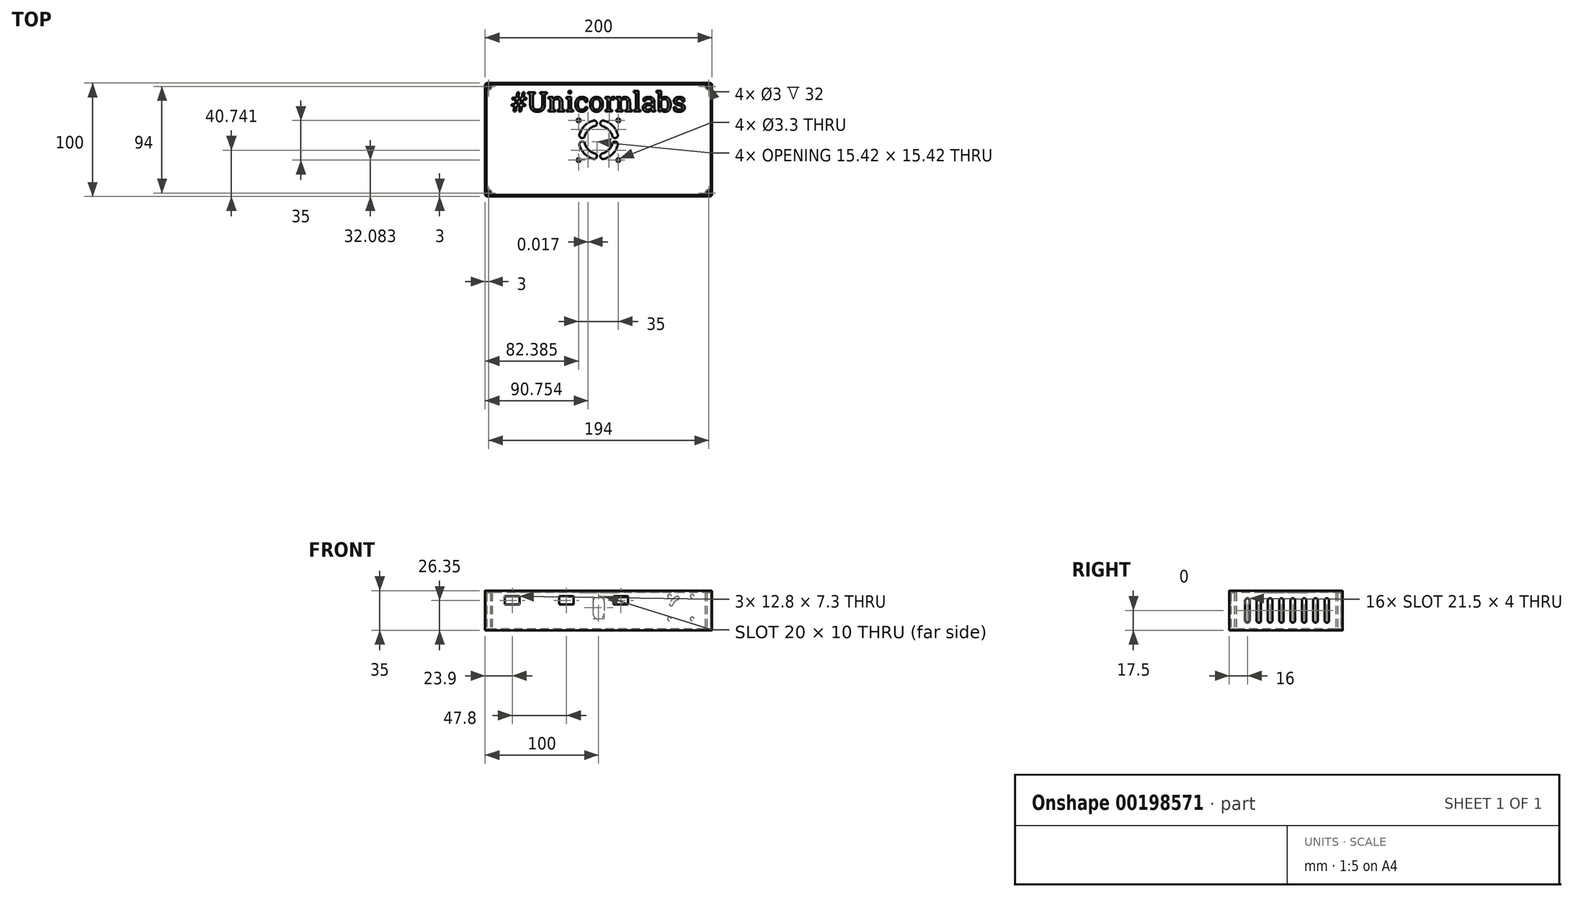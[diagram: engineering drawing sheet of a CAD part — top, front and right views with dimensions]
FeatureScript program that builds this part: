
annotation { "Feature Type Name" : "Feature", "Feature Type Description" : "" }
export const myFeature = defineFeature(function(context is Context, id is Id, definition is map)
    precondition{}
    {
        {
            assignVariable(context, id + "F0", {"name" : "CaseHeight", "anyValue" : 35});
        }
        {
            assignVariable(context, id + "F1", {"name" : "CaseWallThickness", "anyValue" : 1.2});
        }
        {
            assignVariable(context, id + "F2", {"name" : "MetricScrew", "anyValue" : 3});
        }
        {
            var Q0;
            Q0=qCreatedBy(makeId("Top.planeOp"),FACE);
            var sketch = newSketch(context, id + "F3", { "sketchPlane" : qUnion([Q0])});
            skLineSegment(sketch, "E0.bottom", {"start": v(100, 50) * mm, "end": v(-100, 50) * mm});
            skLineSegment(sketch, "E0.top", {"start": v(100, -50) * mm, "end": v(-100, -50) * mm});
            skLineSegment(sketch, "E0.left", {"start": v(100, 50) * mm, "end": v(100, -50) * mm});
            skLineSegment(sketch, "E0.right", {"start": v(-100, 50) * mm, "end": v(-100, -50) * mm});
            skPoint(sketch, "E0.middle", {"position": v(0, 0) * mm});
            skSolve(sketch);
        }
        {
            var Q0;
            Q0=makeQuery(id+"F3.imprint","IMPRINT",FACE,{"disambiguationData":[TD([[makeQuery(id+"F3.imprint","IMPRINT",EDGE,{"derivedFrom":sQuery(id+"F3.wireOp",EDGE,"E0.bottom")}),1.0]])]});
            extrude(context, id + "F4", {"entities" : qUnion([Q0]), "depth" : (getVariable(context, 'CaseHeight')) * mm});
        }
        {
            var Q0;
            Q0=makeQuery(id+"F4.opExtrude","CAP_FACE",FACE,{"disambiguationData":[OSD([sQuery(id+"F3.wireOp",EDGE,"E0.bottom"),sQuery(id+"F3.wireOp",EDGE,"E0.top"),sQuery(id+"F3.wireOp",EDGE,"E0.left"),sQuery(id+"F3.wireOp",EDGE,"E0.right")])],"isStart":false});
            shell(context, id + "F5", {"entities" : qUnion([Q0]), "thickness" : (getVariable(context, 'CaseWallThickness')) * mm});
        }
        {
            var Q0;
            Q0=makeQuery(id+"F5.opShell","OFFSET_FACE",FACE,{"disambiguationData":[OSD([sQuery(id+"F3.wireOp",EDGE,"E0.bottom"),sQuery(id+"F3.wireOp",EDGE,"E0.top"),sQuery(id+"F3.wireOp",EDGE,"E0.left"),sQuery(id+"F3.wireOp",EDGE,"E0.right")])]});
            var sketch = newSketch(context, id + "F6", { "sketchPlane" : qUnion([Q0])});
            skCircle(sketch, "E1", {"center": v(-97, 47) * mm, "radius": 1.5 * mm});
            skCircle(sketch, "E2", {"center": v(97, 47) * mm, "radius": 1.5 * mm});
            skCircle(sketch, "E3", {"center": v(97, -47) * mm, "radius": 1.5 * mm});
            skCircle(sketch, "E4", {"center": v(-97, -47) * mm, "radius": 1.5 * mm});
            skArc(sketch, "E5", {"start": v(-98.8, 44) * mm, "mid": v(-94.88, 44.88) * mm, "end": v(-94, 48.8) * mm});
            skArc(sketch, "E6.MirrorCS", {"start": v(98.8, 44) * mm, "mid": v(94.88, 44.88) * mm, "end": v(94, 48.8) * mm});
            skArc(sketch, "E7.MirrorCS", {"start": v(-98.8, -44) * mm, "mid": v(-94.88, -44.88) * mm, "end": v(-94, -48.8) * mm});
            skArc(sketch, "E8.MirrorCS", {"start": v(98.8, -44) * mm, "mid": v(94.88, -44.88) * mm, "end": v(94, -48.8) * mm});
            skSolve(sketch);
        }
        {
            var Q0;
            Q0=makeQuery(id+"F6.imprint","IMPRINT",FACE,{"disambiguationData":[TD([[makeQuery(id+"F6.imprint","IMPRINT",EDGE,{"derivedFrom":sQuery(id+"F6.wireOp",EDGE,"E1")}),-1.0]])]});
            var Q1;
            Q1=makeQuery(id+"F6.imprint","IMPRINT",FACE,{"disambiguationData":[TD([[makeQuery(id+"F6.imprint","IMPRINT",EDGE,{"derivedFrom":sQuery(id+"F6.wireOp",EDGE,"E2")}),-1.0]])]});
            var Q2;
            Q2=makeQuery(id+"F6.imprint","IMPRINT",FACE,{"disambiguationData":[TD([[makeQuery(id+"F6.imprint","IMPRINT",EDGE,{"derivedFrom":sQuery(id+"F6.wireOp",EDGE,"E3")}),-1.0]])]});
            var Q3;
            Q3=makeQuery(id+"F6.imprint","IMPRINT",FACE,{"disambiguationData":[TD([[makeQuery(id+"F6.imprint","IMPRINT",EDGE,{"derivedFrom":sQuery(id+"F6.wireOp",EDGE,"E4")}),-1.0]])]});
            extrude(context, id + "F7", {"entities" : qUnion([Q0, Q1, Q2, Q3]), "operationType" : NewBodyOperationType.ADD, "depth" : (getVariable(context, 'CaseHeight') - getVariable(context, 'MetricScrew')) * mm});
        }
        {
            var Q0;
            Q0=makeQuery(id+"F7.opExtrude","CAP_FACE",FACE,{"disambiguationData":[OSD([sQuery(id+"F3.wireOp",EDGE,"E0.bottom"),sQuery(id+"F3.wireOp",EDGE,"E0.right"),sQuery(id+"F6.wireOp",EDGE,"E1"),sQuery(id+"F6.wireOp",EDGE,"E5")])],"isStart":false});
            var sketch = newSketch(context, id + "F8", { "sketchPlane" : qUnion([Q0])});
            skPoint(sketch, "E9.0", {"position": v(98.8, -48.8) * mm});
            skPoint(sketch, "E10.0", {"position": v(-98.8, 48.8) * mm});
            skLineSegment(sketch, "E11.bottom", {"start": v(-98.8, 48.8) * mm, "end": v(98.8, 48.8) * mm});
            skLineSegment(sketch, "E11.top", {"start": v(-98.8, -48.8) * mm, "end": v(98.8, -48.8) * mm});
            skLineSegment(sketch, "E11.left", {"start": v(-98.8, 48.8) * mm, "end": v(-98.8, -48.8) * mm});
            skLineSegment(sketch, "E11.right", {"start": v(98.8, 48.8) * mm, "end": v(98.8, -48.8) * mm});
            skCircle(sketch, "E12.0", {"center": v(-97, 47) * mm, "radius": 1.5 * mm});
            skCircle(sketch, "E13.0", {"center": v(97, 47) * mm, "radius": 1.5 * mm});
            skCircle(sketch, "E14.0", {"center": v(97, -47) * mm, "radius": 1.5 * mm});
            skCircle(sketch, "E15.0", {"center": v(-97, -47) * mm, "radius": 1.5 * mm});
            skSolve(sketch);
        }
        {
            var Q0;
            Q0=makeQuery(id+"F8.imprint","IMPRINT",FACE,{"disambiguationData":[TD([[makeQuery(id+"F8.imprint","IMPRINT",EDGE,{"derivedFrom":sQuery(id+"F8.wireOp",EDGE,"E12.0")}),-1.0]])]});
            var Q1;
            {var subQ3=sQuery(id+"F8.wireOp",EDGE,"E11.top");Q1=makeQuery(id+"F8.imprint","IMPRINT",FACE,{"disambiguationData":[TD([[makeQuery(id+"F8.imprint","IMPRINT",EDGE,{"derivedFrom":subQ3}),1.0]])]});}
            extrude(context, id + "F9", {"entities" : qUnion([Q0, Q1]), "depth" : (getVariable(context, 'MetricScrew') / 2) * mm});
        }
        {
            var Q0;
            Q0=makeQuery(id+"F4.opExtrude","SWEPT_FACE",FACE,{"disambiguationData":[OSD([sQuery(id+"F3.wireOp",EDGE,"E0.top")])]});
            var sketch = newSketch(context, id + "F10", { "sketchPlane" : qUnion([Q0])});
            skLineSegment(sketch, "E16.bottom", {"start": v(-69.7, 30) * mm, "end": v(-82.5, 30) * mm});
            skLineSegment(sketch, "E16.top", {"start": v(-69.7, 22.7) * mm, "end": v(-82.5, 22.7) * mm});
            skLineSegment(sketch, "E16.left", {"start": v(-69.7, 30) * mm, "end": v(-69.7, 22.7) * mm});
            skLineSegment(sketch, "E16.right", {"start": v(-82.5, 30) * mm, "end": v(-82.5, 22.7) * mm});
            skPoint(sketch, "E16.middle", {"position": v(-76.1, 26.35) * mm});
            skLineSegment(sketch, "E17.1.0.0", {"start": v(-21.9, 30) * mm, "end": v(-21.9, 22.7) * mm});
            skLineSegment(sketch, "E17.1.0.1", {"start": v(-21.9, 30) * mm, "end": v(-34.7, 30) * mm});
            skLineSegment(sketch, "E17.1.0.2", {"start": v(-34.7, 30) * mm, "end": v(-34.7, 22.7) * mm});
            skLineSegment(sketch, "E17.1.0.3", {"start": v(-21.9, 22.7) * mm, "end": v(-34.7, 22.7) * mm});
            skLineSegment(sketch, "E17.2.0.0", {"start": v(25.9, 30) * mm, "end": v(25.9, 22.7) * mm});
            skLineSegment(sketch, "E17.2.0.1", {"start": v(25.9, 30) * mm, "end": v(13.1, 30) * mm});
            skLineSegment(sketch, "E17.2.0.2", {"start": v(13.1, 30) * mm, "end": v(13.1, 22.7) * mm});
            skLineSegment(sketch, "E17.2.0.3", {"start": v(25.9, 22.7) * mm, "end": v(13.1, 22.7) * mm});
            skLineSegment(sketch, "E17.direction1", {"start": v(-69.7, 22.7) * mm, "end": v(-21.9, 22.7) * mm, "construction": true});
            skSolve(sketch);
        }
        {
            var Q0;
            Q0 = qSketchRegion(id + "F10", true);
            extrude(context, id + "F11", {"entities" : qUnion([Q0]), "operationType" : NewBodyOperationType.REMOVE, "oppositeDirection" : true, "depth" : (getVariable(context, 'CaseWallThickness')) * mm});
        }
        {
            var Q0;
            {var subQ0=sQuery(id+"F3.wireOp",EDGE,"E0.right");var subQ1=sQuery(id+"F3.wireOp",EDGE,"E0.left");var subQ2=sQuery(id+"F3.wireOp",EDGE,"E0.top");var subQ3=sQuery(id+"F3.wireOp",EDGE,"E0.bottom");Q0=makeQuery(id+"F7.boolean.opBoolean","SPLIT",FACE,{"disambiguationData":[TD([makeQuery(id+"F5.opShell","OFFSET_FACE",FACE,{"disambiguationData":[OSD([subQ3])]})])],"derivedFrom":makeQuery(id+"F5.opShell","OFFSET_FACE",FACE,{"disambiguationData":[OSD([subQ3,subQ2,subQ1,subQ0])]})});}
            var sketch = newSketch(context, id + "F12", { "sketchPlane" : qUnion([Q0])});
            skLineSegment(sketch, "E18.bottom", {"start": v(-48.8, -43.8) * mm, "end": v(-93.8, -43.8) * mm, "construction": true});
            skLineSegment(sketch, "E18.top", {"start": v(-48.8, -8.8) * mm, "end": v(-93.8, -8.8) * mm, "construction": true});
            skLineSegment(sketch, "E18.left", {"start": v(-48.8, -43.8) * mm, "end": v(-48.8, -8.8) * mm, "construction": true});
            skLineSegment(sketch, "E18.right", {"start": v(-93.8, -43.8) * mm, "end": v(-93.8, -8.8) * mm, "construction": true});
            skPoint(sketch, "E18.middle", {"position": v(-71.3, -26.3) * mm});
            skLineSegment(sketch, "E19.1.0.0", {"start": v(1.2, -8.8) * mm, "end": v(-43.8, -8.8) * mm, "construction": true});
            skLineSegment(sketch, "E19.1.0.1", {"start": v(1.2, -43.8) * mm, "end": v(-43.8, -43.8) * mm, "construction": true});
            skLineSegment(sketch, "E19.1.0.2", {"start": v(1.2, -43.8) * mm, "end": v(1.2, -8.8) * mm, "construction": true});
            skLineSegment(sketch, "E19.1.0.3", {"start": v(-43.8, -43.8) * mm, "end": v(-43.8, -8.8) * mm, "construction": true});
            skPoint(sketch, "E19.1.0.4", {"position": v(-21.3, -26.3) * mm});
            skLineSegment(sketch, "E19.2.0.0", {"start": v(51.2, -8.8) * mm, "end": v(6.2, -8.8) * mm, "construction": true});
            skLineSegment(sketch, "E19.2.0.1", {"start": v(51.2, -43.8) * mm, "end": v(6.2, -43.8) * mm, "construction": true});
            skLineSegment(sketch, "E19.2.0.2", {"start": v(51.2, -43.8) * mm, "end": v(51.2, -8.8) * mm, "construction": true});
            skLineSegment(sketch, "E19.2.0.3", {"start": v(6.2, -43.8) * mm, "end": v(6.2, -8.8) * mm, "construction": true});
            skPoint(sketch, "E19.2.0.4", {"position": v(28.7, -26.3) * mm});
            skLineSegment(sketch, "E19.direction1", {"start": v(-93.8, -43.8) * mm, "end": v(-43.8, -43.8) * mm, "construction": true});
            skLineSegment(sketch, "E20.bottom", {"start": v(81.2, -3.8) * mm, "end": v(1.2, -3.8) * mm, "construction": true});
            skLineSegment(sketch, "E20.top", {"start": v(81.2, 46.2) * mm, "end": v(1.2, 46.2) * mm, "construction": true});
            skLineSegment(sketch, "E20.left", {"start": v(81.2, -3.8) * mm, "end": v(81.2, 46.2) * mm, "construction": true});
            skLineSegment(sketch, "E20.right", {"start": v(1.2, -3.8) * mm, "end": v(1.2, 46.2) * mm, "construction": true});
            skPoint(sketch, "E20.middle", {"position": v(41.2, 21.2) * mm});
            skCircle(sketch, "E21", {"center": v(-53.8, -38.8) * mm, "radius": 2 * mm, "construction": true});
            skCircle(sketch, "E22", {"center": v(-87.8, -38.8) * mm, "radius": 2 * mm, "construction": true});
            skCircle(sketch, "E23.1.0.0", {"center": v(-37.8, -38.8) * mm, "radius": 2 * mm, "construction": true});
            skCircle(sketch, "E23.1.0.1", {"center": v(-3.8, -38.8) * mm, "radius": 2 * mm, "construction": true});
            skLineSegment(sketch, "E23.direction1", {"start": v(-87.8, -38.8) * mm, "end": v(-37.8, -38.8) * mm, "construction": true});
            skCircle(sketch, "E24.0.2.0", {"center": v(12.2, -38.8) * mm, "radius": 2 * mm, "construction": true});
            skCircle(sketch, "E24.2.2.0", {"center": v(46.2, -38.8) * mm, "radius": 2 * mm, "construction": true});
            skLineSegment(sketch, "E25.bottom", {"start": v(-13.8, 52.2) * mm, "end": v(-98.8, 52.2) * mm, "construction": true});
            skLineSegment(sketch, "E25.top", {"start": v(-13.8, -3.8) * mm, "end": v(-98.8, -3.8) * mm, "construction": true});
            skLineSegment(sketch, "E25.left", {"start": v(-13.8, 52.2) * mm, "end": v(-13.8, -3.8) * mm, "construction": true});
            skLineSegment(sketch, "E25.right", {"start": v(-98.8, 52.2) * mm, "end": v(-98.8, -3.8) * mm, "construction": true});
            skCircle(sketch, "E26", {"center": v(-17.3, 48.7) * mm, "radius": 1.25 * mm, "construction": true});
            skCircle(sketch, "E27", {"center": v(-17.3, -0.3) * mm, "radius": 1.25 * mm, "construction": true});
            skCircle(sketch, "E28", {"center": v(-75.3, 48.7) * mm, "radius": 1.25 * mm, "construction": true});
            skCircle(sketch, "E29", {"center": v(-75.3, -0.3) * mm, "radius": 1.25 * mm, "construction": true});
            skLineSegment(sketch, "E30.bottom", {"start": v(-98.8, 47.03) * mm, "end": v(-84.72, 47.03) * mm, "construction": true});
            skLineSegment(sketch, "E30.top", {"start": v(-98.8, 33) * mm, "end": v(-84.72, 33) * mm, "construction": true});
            skLineSegment(sketch, "E30.left", {"start": v(-98.8, 47.03) * mm, "end": v(-98.8, 33) * mm, "construction": true});
            skLineSegment(sketch, "E30.right", {"start": v(-84.72, 47.03) * mm, "end": v(-84.72, 33) * mm, "construction": true});
            skLineSegment(sketch, "E31.bottom", {"start": v(-98.8, 26.34) * mm, "end": v(-82.63, 26.34) * mm, "construction": true});
            skLineSegment(sketch, "E31.top", {"start": v(-98.8, 15.16) * mm, "end": v(-82.63, 15.16) * mm, "construction": true});
            skLineSegment(sketch, "E31.left", {"start": v(-98.8, 26.34) * mm, "end": v(-98.8, 15.16) * mm, "construction": true});
            skLineSegment(sketch, "E31.right", {"start": v(-82.63, 26.34) * mm, "end": v(-82.63, 15.16) * mm, "construction": true});
            skLineSegment(sketch, "E32.bottom", {"start": v(-98.8, 11.68) * mm, "end": v(-82.2, 11.68) * mm, "construction": true});
            skLineSegment(sketch, "E32.top", {"start": v(-98.8, 2.22) * mm, "end": v(-82.2, 2.22) * mm, "construction": true});
            skLineSegment(sketch, "E32.left", {"start": v(-98.8, 11.68) * mm, "end": v(-98.8, 2.22) * mm, "construction": true});
            skLineSegment(sketch, "E32.right", {"start": v(-82.2, 11.68) * mm, "end": v(-82.2, 2.22) * mm, "construction": true});
            skLineSegment(sketch, "E33.bottom", {"start": v(-95.5, -3.8) * mm, "end": v(-102, -3.8) * mm, "construction": true});
            skLineSegment(sketch, "E33.top", {"start": v(-95.5, -1.49) * mm, "end": v(-102, -1.49) * mm, "construction": true});
            skLineSegment(sketch, "E33.left", {"start": v(-95.5, -3.8) * mm, "end": v(-95.5, -1.49) * mm, "construction": true});
            skLineSegment(sketch, "E33.right", {"start": v(-102, -3.8) * mm, "end": v(-102, -1.49) * mm, "construction": true});
            skSolve(sketch);
        }
        {
            var Q0;
            Q0=makeQuery(id+"F5.opShell","OFFSET_FACE",FACE,{"disambiguationData":[OSD([sQuery(id+"F3.wireOp",EDGE,"E0.bottom")])]});
            var sketch = newSketch(context, id + "F13", { "sketchPlane" : qUnion([Q0])});
            skLineSegment(sketch, "E34.bottom", {"start": v(60, 32.5) * mm, "end": v(85, 32.5) * mm, "construction": true});
            skLineSegment(sketch, "E34.top", {"start": v(60, 7.5) * mm, "end": v(85, 7.5) * mm, "construction": true});
            skLineSegment(sketch, "E34.left", {"start": v(60, 32.5) * mm, "end": v(60, 7.5) * mm, "construction": true});
            skLineSegment(sketch, "E34.right", {"start": v(85, 32.5) * mm, "end": v(85, 7.5) * mm, "construction": true});
            skPoint(sketch, "E34.middle", {"position": v(72.5, 20) * mm});
            skCircle(sketch, "E35", {"center": v(72.5, 20) * mm, "radius": 12.5 * mm});
            skCircle(sketch, "E36", {"center": v(72.5, 20) * mm, "radius": 5 * mm, "construction": true});
            skArc(sketch, "E37", {"start": v(69.5, 28.49) * mm, "mid": v(66.14, 26.36) * mm, "end": v(64.01, 23) * mm, "construction": true});
            skArc(sketch, "E38.1.0", {"start": v(64.01, 17) * mm, "mid": v(66.14, 13.64) * mm, "end": v(69.5, 11.51) * mm, "construction": true});
            skArc(sketch, "E38.2.0", {"start": v(75.5, 11.51) * mm, "mid": v(78.86, 13.64) * mm, "end": v(80.99, 17) * mm, "construction": true});
            skArc(sketch, "E38.3.0", {"start": v(80.99, 23) * mm, "mid": v(78.86, 26.36) * mm, "end": v(75.5, 28.49) * mm, "construction": true});
            skArc(sketch, "E39.0", {"start": v(70, 27.07) * mm, "mid": v(67.2, 25.3) * mm, "end": v(65.43, 22.5) * mm});
            skArc(sketch, "E40.0", {"start": v(69, 29.9) * mm, "mid": v(65.08, 27.42) * mm, "end": v(62.6, 23.5) * mm});
            skArc(sketch, "E41", {"start": v(62.6, 23.5) * mm, "mid": v(63.51, 21.59) * mm, "end": v(65.43, 22.5) * mm});
            skArc(sketch, "E42", {"start": v(70, 27.07) * mm, "mid": v(70.91, 28.99) * mm, "end": v(69, 29.9) * mm});
            skPoint(sketch, "E43", {"position": v(62.5, 30) * mm});
            skPoint(sketch, "E44", {"position": v(82.5, 30) * mm});
            skPoint(sketch, "E45", {"position": v(82.5, 10) * mm});
            skPoint(sketch, "E46", {"position": v(62.5, 10) * mm});
            skLineSegment(sketch, "E47", {"start": v(72.5, 20) * mm, "end": v(72.5, 28.33) * mm, "construction": true});
            skLineSegment(sketch, "E48", {"start": v(72.5, 20) * mm, "end": v(63.9, 20) * mm, "construction": true});
            skSolve(sketch);
        }
        {
            var Q0;
            Q0=makeQuery(id+"F13.imprint","IMPRINT",FACE,{"disambiguationData":[TD([[makeQuery(id+"F13.imprint","IMPRINT",EDGE,{"derivedFrom":sQuery(id+"F13.wireOp",EDGE,"E35")}),-1.0]])]});
            var sketch = newSketch(context, id + "F14", { "sketchPlane" : qUnion([Q0])});
            skLineSegment(sketch, "E49", {"start": v(0, 25) * mm, "end": v(0, 15) * mm});
            skArc(sketch, "E50.0.startCap", {"start": v(-5, 25) * mm, "mid": v(0, 30) * mm, "end": v(5, 25) * mm});
            skArc(sketch, "E50.0.endCap", {"start": v(5, 15) * mm, "mid": v(0, 10) * mm, "end": v(-5, 15) * mm});
            skLineSegment(sketch, "E50.0.left", {"start": v(5, 25) * mm, "end": v(5, 15) * mm});
            skLineSegment(sketch, "E50.0.right", {"start": v(-5, 25) * mm, "end": v(-5, 15) * mm});
            skSolve(sketch);
        }
        {
            var Q0;
            Q0 = qSketchRegion(id + "F14", true);
            extrude(context, id + "F15", {"entities" : qUnion([Q0]), "operationType" : NewBodyOperationType.REMOVE, "oppositeDirection" : true, "depth" : (getVariable(context, 'CaseWallThickness')) * mm});
        }
        {
            var Q0;
            Q0=makeQuery(id+"F4.opExtrude","SWEPT_FACE",FACE,{"disambiguationData":[OSD([sQuery(id+"F3.wireOp",EDGE,"E0.right")])]});
            var sketch = newSketch(context, id + "F16", { "sketchPlane" : qUnion([Q0])});
            skLineSegment(sketch, "E51", {"start": v(-36, 26.25) * mm, "end": v(-36, 8.75) * mm});
            skArc(sketch, "E52.0.startCap", {"start": v(-38, 26.25) * mm, "mid": v(-36, 28.25) * mm, "end": v(-34, 26.25) * mm});
            skArc(sketch, "E52.0.endCap", {"start": v(-34, 8.75) * mm, "mid": v(-36, 6.75) * mm, "end": v(-38, 8.75) * mm});
            skLineSegment(sketch, "E52.0.left", {"start": v(-34, 26.25) * mm, "end": v(-34, 8.75) * mm});
            skLineSegment(sketch, "E52.0.right", {"start": v(-38, 26.25) * mm, "end": v(-38, 8.75) * mm});
            skLineSegment(sketch, "E53.1.0.0", {"start": v(-28, 26.25) * mm, "end": v(-28, 8.75) * mm});
            skLineSegment(sketch, "E53.1.0.1", {"start": v(-24, 26.25) * mm, "end": v(-24, 8.75) * mm});
            skArc(sketch, "E53.1.0.2", {"start": v(-24, 8.75) * mm, "mid": v(-26, 6.75) * mm, "end": v(-28, 8.75) * mm});
            skArc(sketch, "E53.1.0.3", {"start": v(-28, 26.25) * mm, "mid": v(-26, 28.25) * mm, "end": v(-24, 26.25) * mm});
            skLineSegment(sketch, "E53.1.0.4", {"start": v(-26, 26.25) * mm, "end": v(-26, 8.75) * mm});
            skLineSegment(sketch, "E53.2.0.0", {"start": v(-18, 26.25) * mm, "end": v(-18, 8.75) * mm});
            skLineSegment(sketch, "E53.2.0.1", {"start": v(-14, 26.25) * mm, "end": v(-14, 8.75) * mm});
            skArc(sketch, "E53.2.0.2", {"start": v(-14, 8.75) * mm, "mid": v(-16, 6.75) * mm, "end": v(-18, 8.75) * mm});
            skArc(sketch, "E53.2.0.3", {"start": v(-18, 26.25) * mm, "mid": v(-16, 28.25) * mm, "end": v(-14, 26.25) * mm});
            skLineSegment(sketch, "E53.2.0.4", {"start": v(-16, 26.25) * mm, "end": v(-16, 8.75) * mm});
            skLineSegment(sketch, "E53.3.0.0", {"start": v(-8, 26.25) * mm, "end": v(-8, 8.75) * mm});
            skLineSegment(sketch, "E53.3.0.1", {"start": v(-4, 26.25) * mm, "end": v(-4, 8.75) * mm});
            skArc(sketch, "E53.3.0.2", {"start": v(-4, 8.75) * mm, "mid": v(-6, 6.75) * mm, "end": v(-8, 8.75) * mm});
            skArc(sketch, "E53.3.0.3", {"start": v(-8, 26.25) * mm, "mid": v(-6, 28.25) * mm, "end": v(-4, 26.25) * mm});
            skLineSegment(sketch, "E53.3.0.4", {"start": v(-6, 26.25) * mm, "end": v(-6, 8.75) * mm});
            skLineSegment(sketch, "E53.4.0.0", {"start": v(2, 26.25) * mm, "end": v(2, 8.75) * mm});
            skLineSegment(sketch, "E53.4.0.1", {"start": v(6, 26.25) * mm, "end": v(6, 8.75) * mm});
            skArc(sketch, "E53.4.0.2", {"start": v(6, 8.75) * mm, "mid": v(4, 6.75) * mm, "end": v(2, 8.75) * mm});
            skArc(sketch, "E53.4.0.3", {"start": v(2, 26.25) * mm, "mid": v(4, 28.25) * mm, "end": v(6, 26.25) * mm});
            skLineSegment(sketch, "E53.4.0.4", {"start": v(4, 26.25) * mm, "end": v(4, 8.75) * mm});
            skLineSegment(sketch, "E53.5.0.0", {"start": v(12, 26.25) * mm, "end": v(12, 8.75) * mm});
            skLineSegment(sketch, "E53.5.0.1", {"start": v(16, 26.25) * mm, "end": v(16, 8.75) * mm});
            skArc(sketch, "E53.5.0.2", {"start": v(16, 8.75) * mm, "mid": v(14, 6.75) * mm, "end": v(12, 8.75) * mm});
            skArc(sketch, "E53.5.0.3", {"start": v(12, 26.25) * mm, "mid": v(14, 28.25) * mm, "end": v(16, 26.25) * mm});
            skLineSegment(sketch, "E53.5.0.4", {"start": v(14, 26.25) * mm, "end": v(14, 8.75) * mm});
            skLineSegment(sketch, "E53.6.0.0", {"start": v(22, 26.25) * mm, "end": v(22, 8.75) * mm});
            skLineSegment(sketch, "E53.6.0.1", {"start": v(26, 26.25) * mm, "end": v(26, 8.75) * mm});
            skArc(sketch, "E53.6.0.2", {"start": v(26, 8.75) * mm, "mid": v(24, 6.75) * mm, "end": v(22, 8.75) * mm});
            skArc(sketch, "E53.6.0.3", {"start": v(22, 26.25) * mm, "mid": v(24, 28.25) * mm, "end": v(26, 26.25) * mm});
            skLineSegment(sketch, "E53.6.0.4", {"start": v(24, 26.25) * mm, "end": v(24, 8.75) * mm});
            skLineSegment(sketch, "E53.7.0.0", {"start": v(32, 26.25) * mm, "end": v(32, 8.75) * mm});
            skLineSegment(sketch, "E53.7.0.1", {"start": v(36, 26.25) * mm, "end": v(36, 8.75) * mm});
            skArc(sketch, "E53.7.0.2", {"start": v(36, 8.75) * mm, "mid": v(34, 6.75) * mm, "end": v(32, 8.75) * mm});
            skArc(sketch, "E53.7.0.3", {"start": v(32, 26.25) * mm, "mid": v(34, 28.25) * mm, "end": v(36, 26.25) * mm});
            skLineSegment(sketch, "E53.7.0.4", {"start": v(34, 26.25) * mm, "end": v(34, 8.75) * mm});
            skLineSegment(sketch, "E53.direction1", {"start": v(-38, 8.75) * mm, "end": v(-28, 8.75) * mm, "construction": true});
            skSolve(sketch);
        }
        {
            var Q0;
            Q0 = qSketchRegion(id + "F16", true);
            extrude(context, id + "F17", {"entities" : qUnion([Q0]), "operationType" : NewBodyOperationType.REMOVE, "endBound" : BoundingType.THROUGH_ALL, "oppositeDirection" : true, "depth" : 25 * mm});
        }
        {
            var Q0;
            Q0=makeQuery(id+"F4.opExtrude","SWEPT_EDGE",EDGE,{"disambiguationData":[OSD([sQuery(id+"F3.wireOp",EDGE,"E0.bottom"),sQuery(id+"F3.wireOp",EDGE,"E0.right")])]});
            var Q1;
            Q1=makeQuery(id+"F4.opExtrude","SWEPT_EDGE",EDGE,{"disambiguationData":[OSD([sQuery(id+"F3.wireOp",EDGE,"E0.top"),sQuery(id+"F3.wireOp",EDGE,"E0.right")])]});
            var Q2;
            Q2=makeQuery(id+"F4.opExtrude","SWEPT_EDGE",EDGE,{"disambiguationData":[OSD([sQuery(id+"F3.wireOp",EDGE,"E0.top"),sQuery(id+"F3.wireOp",EDGE,"E0.left")])]});
            var Q3;
            Q3=makeQuery(id+"F4.opExtrude","SWEPT_EDGE",EDGE,{"disambiguationData":[OSD([sQuery(id+"F3.wireOp",EDGE,"E0.bottom"),sQuery(id+"F3.wireOp",EDGE,"E0.left")])]});
            fillet(context, id + "F18", {"entities" : qUnion([Q0, Q1, Q2, Q3]), "radius" : 2 * mm, "tangentPropagation" : true, "allowEdgeOverflow" : false});
        }
        {
            var Q0;
            Q0=makeQuery(id+"F9.opExtrude","CAP_FACE",FACE,{"disambiguationData":[OSD([sQuery(id+"F8.wireOp",EDGE,"E11.bottom"),sQuery(id+"F8.wireOp",EDGE,"E11.top"),sQuery(id+"F8.wireOp",EDGE,"E11.left"),sQuery(id+"F8.wireOp",EDGE,"E11.right"),sQuery(id+"F8.wireOp",EDGE,"E12.0"),sQuery(id+"F8.wireOp",EDGE,"E13.0"),sQuery(id+"F8.wireOp",EDGE,"E14.0"),sQuery(id+"F8.wireOp",EDGE,"E15.0")])],"isStart":false});
            var sketch = newSketch(context, id + "F19", { "sketchPlane" : qUnion([Q0])});
            skCircle(sketch, "E54", {"center": v(0, 0) * mm, "radius": 20 * mm});
            skLineSegment(sketch, "E55.bottom", {"start": v(20, 20) * mm, "end": v(-20, 20) * mm, "construction": true});
            skLineSegment(sketch, "E55.top", {"start": v(20, -20) * mm, "end": v(-20, -20) * mm, "construction": true});
            skLineSegment(sketch, "E55.left", {"start": v(20, 20) * mm, "end": v(20, -20) * mm, "construction": true});
            skLineSegment(sketch, "E55.right", {"start": v(-20, 20) * mm, "end": v(-20, -20) * mm, "construction": true});
            skLineSegment(sketch, "E56", {"start": v(-20, 0) * mm, "end": v(20, 0) * mm, "construction": true});
            skLineSegment(sketch, "E57", {"start": v(0, 20) * mm, "end": v(0, -20) * mm, "construction": true});
            skLineSegment(sketch, "E58.0.0", {"start": v(98.8, 48.8) * mm, "end": v(-98.8, 48.8) * mm});
            skLineSegment(sketch, "E58.0.1", {"start": v(-98.8, 48.8) * mm, "end": v(-98.8, -48.8) * mm});
            skLineSegment(sketch, "E58.0.2", {"start": v(-98.8, -48.8) * mm, "end": v(98.8, -48.8) * mm});
            skLineSegment(sketch, "E58.0.3", {"start": v(98.8, -48.8) * mm, "end": v(98.8, 48.8) * mm});
            skArc(sketch, "E59", {"start": v(-4, 14.46) * mm, "mid": v(-10.6, 10.6) * mm, "end": v(-14.46, 4) * mm, "construction": true});
            skArc(sketch, "E60.0", {"start": v(-3.33, 12.05) * mm, "mid": v(-8.84, 8.84) * mm, "end": v(-12.05, 3.33) * mm});
            skArc(sketch, "E61.0", {"start": v(-4.67, 16.87) * mm, "mid": v(-12.37, 12.37) * mm, "end": v(-16.87, 4.67) * mm});
            skArc(sketch, "E62", {"start": v(-3.33, 12.05) * mm, "mid": v(-1.6, 15.12) * mm, "end": v(-4.67, 16.87) * mm});
            skArc(sketch, "E63", {"start": v(-16.87, 4.67) * mm, "mid": v(-15.12, 1.6) * mm, "end": v(-12.05, 3.33) * mm});
            skLineSegment(sketch, "E64", {"start": v(-16.87, 4.67) * mm, "end": v(-12.05, 3.33) * mm, "construction": true});
            skLineSegment(sketch, "E65", {"start": v(-4.67, 16.87) * mm, "end": v(-3.33, 12.05) * mm, "construction": true});
            skPoint(sketch, "E66", {"position": v(-17.62, 17.08) * mm});
            skPoint(sketch, "E67", {"position": v(17.38, 17.08) * mm});
            skPoint(sketch, "E68", {"position": v(17.38, -17.92) * mm});
            skPoint(sketch, "E69", {"position": v(-17.62, -17.92) * mm});
            skArc(sketch, "E70.1.0", {"start": v(-12.06, -3.36) * mm, "mid": v(-15.14, -1.62) * mm, "end": v(-16.88, -4.7) * mm});
            skArc(sketch, "E70.1.1", {"start": v(-14.47, -4.03) * mm, "mid": v(-10.62, -10.64) * mm, "end": v(-4.02, -14.49) * mm, "construction": true});
            skLineSegment(sketch, "E70.1.2", {"start": v(-16.88, -4.7) * mm, "end": v(-12.06, -3.36) * mm, "construction": true});
            skArc(sketch, "E70.1.3", {"start": v(-16.88, -4.7) * mm, "mid": v(-12.4, -12.4) * mm, "end": v(-4.68, -16.9) * mm});
            skArc(sketch, "E70.1.4", {"start": v(-12.06, -3.36) * mm, "mid": v(-8.86, -8.87) * mm, "end": v(-3.35, -12.08) * mm});
            skArc(sketch, "E70.1.5", {"start": v(-4.68, -16.9) * mm, "mid": v(-1.6, -15.15) * mm, "end": v(-3.35, -12.08) * mm});
            skLineSegment(sketch, "E70.1.6", {"start": v(-4.68, -16.9) * mm, "end": v(-3.35, -12.08) * mm, "construction": true});
            skArc(sketch, "E70.2.0", {"start": v(3.35, -12.1) * mm, "mid": v(1.6, -15.17) * mm, "end": v(4.68, -16.91) * mm});
            skArc(sketch, "E70.2.1", {"start": v(4.01, -14.5) * mm, "mid": v(10.62, -10.65) * mm, "end": v(14.47, -4.05) * mm, "construction": true});
            skLineSegment(sketch, "E70.2.2", {"start": v(4.68, -16.91) * mm, "end": v(3.35, -12.1) * mm, "construction": true});
            skArc(sketch, "E70.2.3", {"start": v(4.68, -16.91) * mm, "mid": v(12.39, -12.42) * mm, "end": v(16.88, -4.71) * mm});
            skArc(sketch, "E70.2.4", {"start": v(3.35, -12.1) * mm, "mid": v(8.85, -8.89) * mm, "end": v(12.06, -3.38) * mm});
            skArc(sketch, "E70.2.5", {"start": v(16.88, -4.71) * mm, "mid": v(15.14, -1.64) * mm, "end": v(12.06, -3.38) * mm});
            skLineSegment(sketch, "E70.2.6", {"start": v(16.88, -4.71) * mm, "end": v(12.06, -3.38) * mm, "construction": true});
            skArc(sketch, "E70.3.0", {"start": v(12.08, 3.32) * mm, "mid": v(15.15, 1.57) * mm, "end": v(16.9, 4.65) * mm});
            skArc(sketch, "E70.3.1", {"start": v(14.49, 3.98) * mm, "mid": v(10.64, 10.59) * mm, "end": v(4.03, 14.44) * mm, "construction": true});
            skLineSegment(sketch, "E70.3.2", {"start": v(16.9, 4.65) * mm, "end": v(12.08, 3.32) * mm, "construction": true});
            skArc(sketch, "E70.3.3", {"start": v(16.9, 4.65) * mm, "mid": v(12.4, 12.36) * mm, "end": v(4.7, 16.85) * mm});
            skArc(sketch, "E70.3.4", {"start": v(12.08, 3.32) * mm, "mid": v(8.87, 8.82) * mm, "end": v(3.36, 12.03) * mm});
            skArc(sketch, "E70.3.5", {"start": v(4.7, 16.85) * mm, "mid": v(1.62, 15.1) * mm, "end": v(3.36, 12.03) * mm});
            skLineSegment(sketch, "E70.3.6", {"start": v(4.7, 16.85) * mm, "end": v(3.36, 12.03) * mm, "construction": true});
            skPoint(sketch, "E70.center", {"position": v(0, -0.02) * mm});
            skSolve(sketch);
        }
        {
            var Q0;
            Q0=makeQuery(id+"F13.imprint","IMPRINT",FACE,{"disambiguationData":[TD([[makeQuery(id+"F13.imprint","IMPRINT",EDGE,{"derivedFrom":sQuery(id+"F13.wireOp",EDGE,"E39.0")}),-1.0]])]});
            extrude(context, id + "F20", {"entities" : qUnion([Q0]), "operationType" : NewBodyOperationType.REMOVE, "oppositeDirection" : true, "depth" : (getVariable(context, 'CaseWallThickness')) * mm});
        }
        {
            var Q0;
            Q0=makeQuery(id+"F4.opExtrude","CAP_FACE",FACE,{"disambiguationData":[OSD([sQuery(id+"F3.wireOp",EDGE,"E0.bottom"),sQuery(id+"F3.wireOp",EDGE,"E0.top"),sQuery(id+"F3.wireOp",EDGE,"E0.left"),sQuery(id+"F3.wireOp",EDGE,"E0.right")])],"isStart":false});
            cPlane(context, id + "F21", {"entities" : qUnion([Q0]), "cplaneType" : CPlaneType.OFFSET, "offset" : 15 * mm, "oppositeDirection" : true, "width" : 150 * mm, "height" : 150 * mm});
        }
        {
            var Q0;
            Q0=qCreatedBy(id+"F21.planeOp",FACE);
            var sketch = newSketch(context, id + "F22", { "sketchPlane" : qUnion([Q0])});
            skPoint(sketch, "E71.0", {"position": v(72.5, 48.8) * mm});
            skLineSegment(sketch, "E72", {"start": v(72.5, 48.8) * mm, "end": v(72.5, 70) * mm, "construction": true});
            skSolve(sketch);
        }
        {
            var Q0;
            Q0=sQuery(id+"F13.wireOp",VERTEX,"E43");
            var Q1;
            Q1=sQuery(id+"F13.wireOp",VERTEX,"E44");
            var Q2;
            Q2=sQuery(id+"F13.wireOp",VERTEX,"E45");
            var Q3;
            Q3=sQuery(id+"F13.wireOp",VERTEX,"E46");
            var Q4;
            Q4=makeQuery(id+"F4.opExtrude","SWEPT_BODY",BODY,{"disambiguationData":[OSD([sQuery(id+"F3.wireOp",EDGE,"E0.bottom"),sQuery(id+"F3.wireOp",EDGE,"E0.top"),sQuery(id+"F3.wireOp",EDGE,"E0.left"),sQuery(id+"F3.wireOp",EDGE,"E0.right")])]});
            hole(context, id + "F23", {"style" : HoleStyle.SIMPLE, "endStyle" : HoleEndStyle.BLIND, "standardTappedOrClearance" : lookupTablePath({ "standard" : "ISO", "fit" : "Normal", "size" : "M3", "type" : "Clearance" }), "standardBlindInLast" : lookupTablePath({ "fit" : "Standard", "standard" : "ISO", "size" : "M3", "type" : "Clearance" }), "holeDiameter" : 3.3 * mm, "holeDepth" : (getVariable(context, 'CaseWallThickness')) * mm, "startFromSketch" : true, "locations" : qUnion([Q0, Q1, Q2, Q3]), "scope" : qUnion([Q4])});
        }
        {
            var Q0;
            Q0=makeQuery(id+"F19.imprint","IMPRINT",FACE,{"disambiguationData":[TD([[makeQuery(id+"F19.imprint","IMPRINT",EDGE,{"derivedFrom":sQuery(id+"F19.wireOp",EDGE,"E60.0")}),-1.0]])]});
            var Q1;
            Q1=makeQuery(id+"F19.imprint","IMPRINT",FACE,{"disambiguationData":[TD([[makeQuery(id+"F19.imprint","IMPRINT",EDGE,{"derivedFrom":sQuery(id+"F19.wireOp",EDGE,"E70.3.0")}),1.0]])]});
            var Q2;
            Q2=makeQuery(id+"F19.imprint","IMPRINT",FACE,{"disambiguationData":[TD([[makeQuery(id+"F19.imprint","IMPRINT",EDGE,{"derivedFrom":sQuery(id+"F19.wireOp",EDGE,"E70.2.0")}),1.0]])]});
            var Q3;
            Q3=makeQuery(id+"F19.imprint","IMPRINT",FACE,{"disambiguationData":[TD([[makeQuery(id+"F19.imprint","IMPRINT",EDGE,{"derivedFrom":sQuery(id+"F19.wireOp",EDGE,"E70.1.0")}),1.0]])]});
            extrude(context, id + "F24", {"entities" : qUnion([Q0, Q1, Q2, Q3]), "operationType" : NewBodyOperationType.REMOVE, "oppositeDirection" : true, "depth" : (getVariable(context, 'MetricScrew') / 2) * mm});
        }
        {
            var Q0;
            Q0=sQuery(id+"F19.wireOp",VERTEX,"E66");
            var Q1;
            Q1=sQuery(id+"F19.wireOp",VERTEX,"E67");
            var Q2;
            Q2=sQuery(id+"F19.wireOp",VERTEX,"E68");
            var Q3;
            Q3=sQuery(id+"F19.wireOp",VERTEX,"E69");
            var Q4;
            Q4=makeQuery(id+"F9.opExtrude","SWEPT_BODY",BODY,{"disambiguationData":[OSD([sQuery(id+"F8.wireOp",EDGE,"E11.bottom"),sQuery(id+"F8.wireOp",EDGE,"E11.top"),sQuery(id+"F8.wireOp",EDGE,"E11.left"),sQuery(id+"F8.wireOp",EDGE,"E11.right"),sQuery(id+"F8.wireOp",EDGE,"E12.0"),sQuery(id+"F8.wireOp",EDGE,"E13.0"),sQuery(id+"F8.wireOp",EDGE,"E14.0"),sQuery(id+"F8.wireOp",EDGE,"E15.0")])]});
            hole(context, id + "F25", {"style" : HoleStyle.SIMPLE, "endStyle" : HoleEndStyle.BLIND, "standardTappedOrClearance" : lookupTablePath({ "standard" : "ISO", "fit" : "Normal", "size" : "M3", "type" : "Clearance" }), "standardBlindInLast" : lookupTablePath({ "fit" : "Standard", "standard" : "ISO", "size" : "M3", "type" : "Clearance" }), "holeDiameter" : 3.3 * mm, "holeDepth" : (getVariable(context, 'MetricScrew') / 2) * mm, "startFromSketch" : true, "locations" : qUnion([Q0, Q1, Q2, Q3]), "scope" : qUnion([Q4])});
        }
        {
            var Q0;
            Q0=makeQuery(id+"F9.opExtrude","CAP_FACE",FACE,{"disambiguationData":[OSD([sQuery(id+"F8.wireOp",EDGE,"E11.bottom"),sQuery(id+"F8.wireOp",EDGE,"E11.top"),sQuery(id+"F8.wireOp",EDGE,"E11.left"),sQuery(id+"F8.wireOp",EDGE,"E11.right"),sQuery(id+"F8.wireOp",EDGE,"E12.0"),sQuery(id+"F8.wireOp",EDGE,"E13.0"),sQuery(id+"F8.wireOp",EDGE,"E14.0"),sQuery(id+"F8.wireOp",EDGE,"E15.0")])],"isStart":false});
            var sketch = newSketch(context, id + "F26", { "sketchPlane" : qUnion([Q0])});
            skText(sketch, "E73", { "text": "#Unicornlabs", "fontName": "RobotoSlab-Regular.ttf"});
            skLineSegment(sketch, "E74.0.0", {"start": v(98.8, 48.8) * mm, "end": v(-98.8, 48.8) * mm});
            skLineSegment(sketch, "E74.0.1", {"start": v(-98.8, 48.8) * mm, "end": v(-98.8, -48.8) * mm});
            skLineSegment(sketch, "E74.0.2", {"start": v(-98.8, -48.8) * mm, "end": v(98.8, -48.8) * mm});
            skLineSegment(sketch, "E74.0.3", {"start": v(98.8, -48.8) * mm, "end": v(98.8, 48.8) * mm});
            const initialGuessF26  = {"E73": [-0.0775, 0.02488, 1, 0, 0.01727]};
            skSetInitialGuess(sketch, initialGuessF26);
            skSolve(sketch);
        }
        {
            var Q0;
            Q0=makeQuery(id+"F26.imprint","IMPRINT",FACE,{"disambiguationData":[TD([[makeQuery(id+"F26.imprint","IMPRINT",EDGE,{"derivedFrom":sQuery(id+"F26.wireOp",EDGE,"E73.sketch_text.stroke-32")}),-1.0]])]});
            var Q1;
            Q1=makeQuery(id+"F26.imprint","IMPRINT",FACE,{"disambiguationData":[TD([[makeQuery(id+"F26.imprint","IMPRINT",EDGE,{"derivedFrom":sQuery(id+"F26.wireOp",EDGE,"E73.sketch_text.stroke-0")}),-1.0]])]});
            var Q2;
            Q2=makeQuery(id+"F26.imprint","IMPRINT",FACE,{"disambiguationData":[TD([[makeQuery(id+"F26.imprint","IMPRINT",EDGE,{"derivedFrom":sQuery(id+"F26.wireOp",EDGE,"E73.sketch_text.stroke-56")}),-1.0]])]});
            var Q3;
            Q3=makeQuery(id+"F26.imprint","IMPRINT",FACE,{"disambiguationData":[TD([[makeQuery(id+"F26.imprint","IMPRINT",EDGE,{"derivedFrom":sQuery(id+"F26.wireOp",EDGE,"E73.sketch_text.stroke-82")}),-1.0]])]});
            var Q4;
            Q4=makeQuery(id+"F26.imprint","IMPRINT",FACE,{"disambiguationData":[TD([[makeQuery(id+"F26.imprint","IMPRINT",EDGE,{"derivedFrom":sQuery(id+"F26.wireOp",EDGE,"E73.sketch_text.stroke-92")}),-1.0]])]});
            var Q5;
            Q5=makeQuery(id+"F26.imprint","IMPRINT",FACE,{"disambiguationData":[TD([[makeQuery(id+"F26.imprint","IMPRINT",EDGE,{"derivedFrom":sQuery(id+"F26.wireOp",EDGE,"E73.sketch_text.stroke-96")}),-1.0]])]});
            var Q6;
            Q6=makeQuery(id+"F26.imprint","IMPRINT",FACE,{"disambiguationData":[TD([[makeQuery(id+"F26.imprint","IMPRINT",EDGE,{"derivedFrom":sQuery(id+"F26.wireOp",EDGE,"E73.sketch_text.stroke-119")}),-1.0]])]});
            var Q7;
            Q7=makeQuery(id+"F26.imprint","IMPRINT",FACE,{"disambiguationData":[TD([[makeQuery(id+"F26.imprint","IMPRINT",EDGE,{"derivedFrom":sQuery(id+"F26.wireOp",EDGE,"E73.sketch_text.stroke-139")}),-1.0]])]});
            var Q8;
            Q8=makeQuery(id+"F26.imprint","IMPRINT",FACE,{"disambiguationData":[TD([[makeQuery(id+"F26.imprint","IMPRINT",EDGE,{"derivedFrom":sQuery(id+"F26.wireOp",EDGE,"E73.sketch_text.stroke-158")}),-1.0]])]});
            var Q9;
            Q9=makeQuery(id+"F26.imprint","IMPRINT",FACE,{"disambiguationData":[TD([[makeQuery(id+"F26.imprint","IMPRINT",EDGE,{"derivedFrom":sQuery(id+"F26.wireOp",EDGE,"E73.sketch_text.stroke-184")}),-1.0]])]});
            var Q10;
            Q10=makeQuery(id+"F26.imprint","IMPRINT",FACE,{"disambiguationData":[TD([[makeQuery(id+"F26.imprint","IMPRINT",EDGE,{"derivedFrom":sQuery(id+"F26.wireOp",EDGE,"E73.sketch_text.stroke-194")}),-1.0]])]});
            var Q11;
            Q11=makeQuery(id+"F26.imprint","IMPRINT",FACE,{"disambiguationData":[TD([[makeQuery(id+"F26.imprint","IMPRINT",EDGE,{"derivedFrom":sQuery(id+"F26.wireOp",EDGE,"E73.sketch_text.stroke-229")}),-1.0]])]});
            var Q12;
            Q12=makeQuery(id+"F26.imprint","IMPRINT",FACE,{"disambiguationData":[TD([[makeQuery(id+"F26.imprint","IMPRINT",EDGE,{"derivedFrom":sQuery(id+"F26.wireOp",EDGE,"E73.sketch_text.stroke-255")}),-1.0]])]});
            extrude(context, id + "F27", {"entities" : qUnion([Q0, Q1, Q2, Q3, Q4, Q5, Q6, Q7, Q8, Q9, Q10, Q11, Q12]), "operationType" : NewBodyOperationType.REMOVE, "oppositeDirection" : true, "depth" : .6 * mm});
        }
    });
